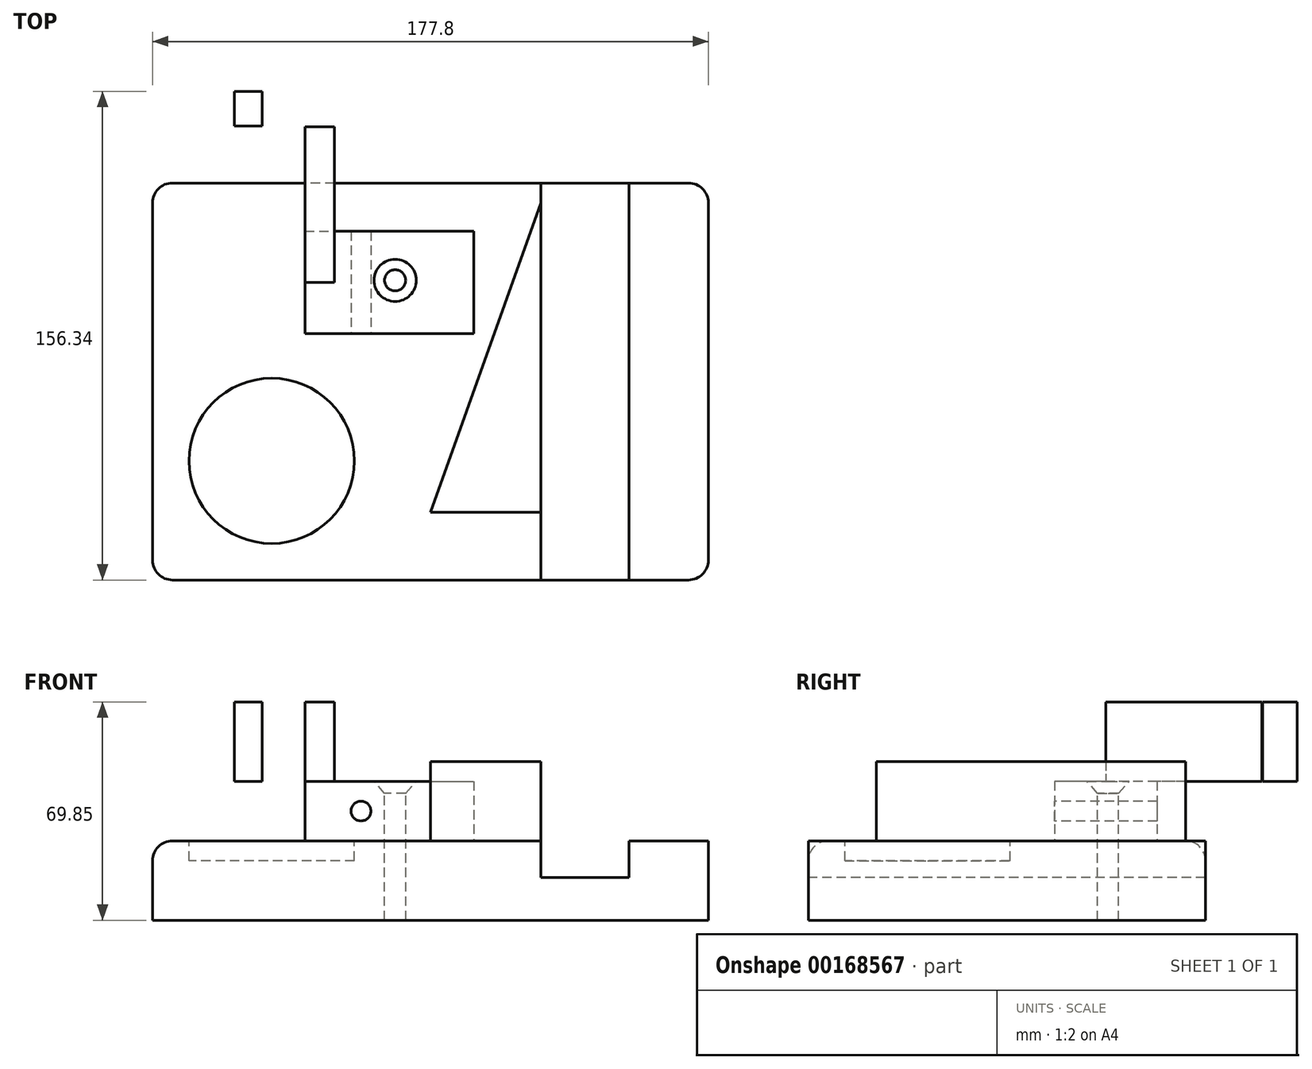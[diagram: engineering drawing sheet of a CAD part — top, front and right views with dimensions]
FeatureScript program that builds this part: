
annotation { "Feature Type Name" : "Feature", "Feature Type Description" : "" }
export const myFeature = defineFeature(function(context is Context, id is Id, definition is map)
    precondition{}
    {
        {
            var Q0;
            Q0=qCreatedBy(makeId("Top.planeOp"),FACE);
            var sketch = newSketch(context, id + "F0", { "sketchPlane" : qUnion([Q0])});
            skLineSegment(sketch, "E0.bottom", {"start": v(82.55, -63.5) * mm, "end": v(-82.55, -63.5) * mm});
            skLineSegment(sketch, "E0.top", {"start": v(82.55, 63.5) * mm, "end": v(-82.55, 63.5) * mm});
            skLineSegment(sketch, "E0.left", {"start": v(88.9, -57.15) * mm, "end": v(88.9, 57.15) * mm});
            skLineSegment(sketch, "E0.right", {"start": v(-88.9, -57.15) * mm, "end": v(-88.9, 57.15) * mm});
            skPoint(sketch, "E0.middle", {"position": v(0, 0) * mm});
            skPoint(sketch, "E1.visualSharp", {"position": v(-88.9, -63.5) * mm});
            skArc(sketch, "E1.filletArc", {"start": v(-88.9, -57.15) * mm, "mid": v(-87.04, -61.64) * mm, "end": v(-82.55, -63.5) * mm});
            skPoint(sketch, "E2.visualSharp", {"position": v(88.9, -63.5) * mm});
            skArc(sketch, "E2.filletArc", {"start": v(82.55, -63.5) * mm, "mid": v(87.04, -61.64) * mm, "end": v(88.9, -57.15) * mm});
            skPoint(sketch, "E3.visualSharp", {"position": v(88.9, 63.5) * mm});
            skArc(sketch, "E3.filletArc", {"start": v(88.9, 57.15) * mm, "mid": v(87.04, 61.64) * mm, "end": v(82.55, 63.5) * mm});
            skPoint(sketch, "E4.visualSharp", {"position": v(-88.9, 63.5) * mm});
            skArc(sketch, "E4.filletArc", {"start": v(-82.55, 63.5) * mm, "mid": v(-87.04, 61.64) * mm, "end": v(-88.9, 57.15) * mm});
            skSolve(sketch);
        }
        {
            var Q0;
            Q0=makeQuery(id+"F0.imprint","IMPRINT",FACE,{"disambiguationData":[TD([[makeQuery(id+"F0.imprint","IMPRINT",EDGE,{"derivedFrom":sQuery(id+"F0.wireOp",EDGE,"E0.bottom")}),-1.0]])]});
            extrude(context, id + "F1", {"entities" : qUnion([Q0]), "depth" : 25.4 * mm});
        }
        {
            var Q0;
            Q0=makeQuery(id+"F1.opExtrude","CAP_FACE",FACE,{"disambiguationData":[OSD([sQuery(id+"F0.wireOp",EDGE,"E0.bottom"),sQuery(id+"F0.wireOp",EDGE,"E0.top"),sQuery(id+"F0.wireOp",EDGE,"E0.left"),sQuery(id+"F0.wireOp",EDGE,"E0.right"),sQuery(id+"F0.wireOp",EDGE,"E1.filletArc"),sQuery(id+"F0.wireOp",EDGE,"E2.filletArc"),sQuery(id+"F0.wireOp",EDGE,"E3.filletArc"),sQuery(id+"F0.wireOp",EDGE,"E4.filletArc")])],"isStart":false});
            var sketch = newSketch(context, id + "F2", { "sketchPlane" : qUnion([Q0])});
            skCircle(sketch, "E5", {"center": v(-50.8, -25.4) * mm, "radius": 26.45 * mm});
            skSolve(sketch);
        }
        {
            var Q0;
            Q0 = qSketchRegion(id + "F2", true);
            extrude(context, id + "F3", {"entities" : qUnion([Q0]), "operationType" : NewBodyOperationType.REMOVE, "oppositeDirection" : true, "depth" : 6.35 * mm});
        }
        {
            var Q0;
            Q0=makeQuery(id+"F1.opExtrude","SWEPT_FACE",FACE,{"disambiguationData":[OSD([sQuery(id+"F0.wireOp",EDGE,"E0.bottom")])]});
            var sketch = newSketch(context, id + "F4", { "sketchPlane" : qUnion([Q0])});
            skLineSegment(sketch, "E6.bottom", {"start": v(63.56, 13.67) * mm, "end": v(35.33, 13.67) * mm});
            skLineSegment(sketch, "E6.top", {"start": v(63.56, 37.13) * mm, "end": v(35.33, 37.13) * mm});
            skLineSegment(sketch, "E6.left", {"start": v(63.56, 13.67) * mm, "end": v(63.56, 37.13) * mm});
            skLineSegment(sketch, "E6.right", {"start": v(35.33, 13.67) * mm, "end": v(35.33, 37.13) * mm});
            skPoint(sketch, "E6.middle", {"position": v(49.44, 25.4) * mm});
            skSolve(sketch);
        }
        {
            var Q0;
            {var subQ0=sQuery(id+"F4.wireOp",EDGE,"E6.bottom");Q0=makeQuery(id+"F4.imprint","IMPRINT",FACE,{"disambiguationData":[TD([[makeQuery(id+"F4.imprint","IMPRINT",EDGE,{"derivedFrom":subQ0}),-1.0]])]});}
            extrude(context, id + "F5", {"entities" : qUnion([Q0]), "operationType" : NewBodyOperationType.REMOVE, "oppositeDirection" : true, "depth" : 127 * mm});
        }
        {
            var Q0;
            {var subQ0=sQuery(id+"F0.wireOp",EDGE,"E1.filletArc");var subQ1=sQuery(id+"F0.wireOp",EDGE,"E0.right");var subQ2=sQuery(id+"F0.wireOp",EDGE,"E0.top");var subQ3=sQuery(id+"F0.wireOp",EDGE,"E0.bottom");var subQ4=sQuery(id+"F0.wireOp",EDGE,"E4.filletArc");Q0=makeQuery(id+"F5.boolean.opBoolean","SPLIT",FACE,{"disambiguationData":[TD([makeQuery(id+"F1.opExtrude","SWEPT_FACE",FACE,{"disambiguationData":[OSD([subQ1])]})])],"derivedFrom":makeQuery(id+"F1.opExtrude","CAP_FACE",FACE,{"disambiguationData":[OSD([subQ3,subQ2,sQuery(id+"F0.wireOp",EDGE,"E0.left"),subQ1,subQ0,sQuery(id+"F0.wireOp",EDGE,"E2.filletArc"),sQuery(id+"F0.wireOp",EDGE,"E3.filletArc"),subQ4])],"isStart":false})});}
            var sketch = newSketch(context, id + "F6", { "sketchPlane" : qUnion([Q0])});
            skLineSegment(sketch, "E7.bottom", {"start": v(-40.18, 48.04) * mm, "end": v(13.9, 48.04) * mm});
            skLineSegment(sketch, "E7.top", {"start": v(-40.18, 15.3) * mm, "end": v(13.9, 15.3) * mm});
            skLineSegment(sketch, "E7.left", {"start": v(-40.18, 48.04) * mm, "end": v(-40.18, 15.3) * mm});
            skLineSegment(sketch, "E7.right", {"start": v(13.9, 48.04) * mm, "end": v(13.9, 15.3) * mm});
            skSolve(sketch);
        }
        {
            var Q0;
            Q0=makeQuery(id+"F6.imprint","IMPRINT",FACE,{"disambiguationData":[TD([[makeQuery(id+"F6.imprint","IMPRINT",EDGE,{"derivedFrom":sQuery(id+"F6.wireOp",EDGE,"E7.bottom")}),-1.0]])]});
            extrude(context, id + "F7", {"entities" : qUnion([Q0]), "operationType" : NewBodyOperationType.ADD, "depth" : 19.05 * mm});
        }
        {
            var Q0;
            {var subQ0=sQuery(id+"F0.wireOp",EDGE,"E0.bottom");var subQ1=sQuery(id+"F0.wireOp",EDGE,"E1.filletArc");Q0=makeQuery(id+"F5.boolean.opBoolean","SPLIT",EDGE,{"disambiguationData":[TD([makeQuery(id+"F1.opExtrude","SWEPT_FACE",FACE,{"disambiguationData":[OSD([subQ1])]})])],"derivedFrom":makeQuery(id+"F1.opExtrude","CAP_EDGE",EDGE,{"disambiguationData":[OSD([subQ0])],"isStart":false})});}
            fillet(context, id + "F8", {"entities" : qUnion([Q0]), "radius" : 6.35 * mm, "tangentPropagation" : true, "allowEdgeOverflow" : false});
        }
        {
            var Q0;
            Q0=makeQuery(id+"F7.opExtrude","CAP_FACE",FACE,{"disambiguationData":[OSD([sQuery(id+"F6.wireOp",EDGE,"E7.bottom"),sQuery(id+"F6.wireOp",EDGE,"E7.top"),sQuery(id+"F6.wireOp",EDGE,"E7.left"),sQuery(id+"F6.wireOp",EDGE,"E7.right")])],"isStart":false});
            var sketch = newSketch(context, id + "F9", { "sketchPlane" : qUnion([Q0])});
            skPoint(sketch, "E8", {"position": v(-11.3, 32.36) * mm});
            skSolve(sketch);
        }
        {
            var Q0;
            Q0=sQuery(id+"F9.wireOp",VERTEX,"E8");
            var Q1;
            Q1=makeQuery(id+"F1.opExtrude","SWEPT_BODY",BODY,{"disambiguationData":[OSD([sQuery(id+"F0.wireOp",EDGE,"E0.bottom"),sQuery(id+"F0.wireOp",EDGE,"E0.top"),sQuery(id+"F0.wireOp",EDGE,"E0.left"),sQuery(id+"F0.wireOp",EDGE,"E0.right"),sQuery(id+"F0.wireOp",EDGE,"E1.filletArc"),sQuery(id+"F0.wireOp",EDGE,"E2.filletArc"),sQuery(id+"F0.wireOp",EDGE,"E3.filletArc"),sQuery(id+"F0.wireOp",EDGE,"E4.filletArc")])]});
            hole(context, id + "F10", {"style" : HoleStyle.C_SINK, "endStyle" : HoleEndStyle.THROUGH, "holeDiameter" : 6.76 * mm, "cSinkDiameter" : 13.5 * mm, "cSinkAngle" : 82 * degree, "locations" : qUnion([Q0]), "scope" : qUnion([Q1]), "isTappedThrough" : true});
        }
        {
            var Q0;
            Q0=makeQuery(id+"F7.opExtrude","SWEPT_FACE",FACE,{"disambiguationData":[OSD([sQuery(id+"F6.wireOp",EDGE,"E7.top")])]});
            var sketch = newSketch(context, id + "F11", { "sketchPlane" : qUnion([Q0])});
            skPoint(sketch, "E9", {"position": v(-22.24, 34.93) * mm});
            skPoint(sketch, "E9.positionSnap0", {"position": v(-40.18, 34.93) * mm});
            skSolve(sketch);
        }
        {
            var Q0;
            Q0=sQuery(id+"F11.wireOp",VERTEX,"E9");
            var Q1;
            Q1=makeQuery(id+"F1.opExtrude","SWEPT_BODY",BODY,{"disambiguationData":[OSD([sQuery(id+"F0.wireOp",EDGE,"E0.bottom"),sQuery(id+"F0.wireOp",EDGE,"E0.top"),sQuery(id+"F0.wireOp",EDGE,"E0.left"),sQuery(id+"F0.wireOp",EDGE,"E0.right"),sQuery(id+"F0.wireOp",EDGE,"E1.filletArc"),sQuery(id+"F0.wireOp",EDGE,"E2.filletArc"),sQuery(id+"F0.wireOp",EDGE,"E3.filletArc"),sQuery(id+"F0.wireOp",EDGE,"E4.filletArc")])]});
            hole(context, id + "F12", {"style" : HoleStyle.SIMPLE, "endStyle" : HoleEndStyle.THROUGH, "holeDiameter" : 6.35 * mm, "locations" : qUnion([Q0]), "scope" : qUnion([Q1]), "isTappedThrough" : true});
        }
        {
            var Q0;
            {var subQ0=sQuery(id+"F0.wireOp",EDGE,"E1.filletArc");var subQ1=sQuery(id+"F0.wireOp",EDGE,"E0.right");var subQ2=sQuery(id+"F0.wireOp",EDGE,"E0.top");var subQ3=sQuery(id+"F0.wireOp",EDGE,"E0.bottom");var subQ4=sQuery(id+"F0.wireOp",EDGE,"E4.filletArc");Q0=makeQuery(id+"F5.boolean.opBoolean","SPLIT",FACE,{"disambiguationData":[TD([makeQuery(id+"F1.opExtrude","SWEPT_FACE",FACE,{"disambiguationData":[OSD([subQ1])]})])],"derivedFrom":makeQuery(id+"F1.opExtrude","CAP_FACE",FACE,{"disambiguationData":[OSD([subQ3,subQ2,sQuery(id+"F0.wireOp",EDGE,"E0.left"),subQ1,subQ0,sQuery(id+"F0.wireOp",EDGE,"E2.filletArc"),sQuery(id+"F0.wireOp",EDGE,"E3.filletArc"),subQ4])],"isStart":false})});}
            var sketch = newSketch(context, id + "F13", { "sketchPlane" : qUnion([Q0])});
            skLineSegment(sketch, "E10", {"start": v(0, -41.78) * mm, "end": v(35.33, 57.15) * mm});
            skLineSegment(sketch, "E11", {"start": v(0, -41.78) * mm, "end": v(35.33, -41.78) * mm});
            skLineSegment(sketch, "E12", {"start": v(35.33, -41.78) * mm, "end": v(35.33, 57.15) * mm});
            skSolve(sketch);
        }
        {
            var Q0;
            Q0=makeQuery(id+"F13.imprint","IMPRINT",FACE,{"disambiguationData":[TD([[makeQuery(id+"F13.imprint","IMPRINT",EDGE,{"derivedFrom":sQuery(id+"F13.wireOp",EDGE,"E10")}),-1.0]])]});
            extrude(context, id + "F16", {"entities" : qUnion([Q0]), "operationType" : NewBodyOperationType.ADD, "depth" : 25.4 * mm});
        }
        {
            var Q0;
            Q0=makeQuery(id+"F7.opExtrude","CAP_FACE",FACE,{"disambiguationData":[OSD([sQuery(id+"F6.wireOp",EDGE,"E7.bottom"),sQuery(id+"F6.wireOp",EDGE,"E7.top"),sQuery(id+"F6.wireOp",EDGE,"E7.left"),sQuery(id+"F6.wireOp",EDGE,"E7.right")])],"isStart":false});
            var sketch = newSketch(context, id + "F14", { "sketchPlane" : qUnion([Q0])});
            skLineSegment(sketch, "E13.bottom", {"start": v(-62.77, 81.78) * mm, "end": v(-53.87, 81.78) * mm});
            skLineSegment(sketch, "E13.top", {"start": v(-62.77, 92.84) * mm, "end": v(-53.87, 92.84) * mm});
            skLineSegment(sketch, "E13.left", {"start": v(-62.77, 81.78) * mm, "end": v(-62.77, 92.84) * mm});
            skLineSegment(sketch, "E13.right", {"start": v(-53.87, 81.78) * mm, "end": v(-53.87, 92.84) * mm});
            skLineSegment(sketch, "E14.bottom", {"start": v(-30.7, 81.52) * mm, "end": v(-40.18, 81.52) * mm});
            skLineSegment(sketch, "E14.top", {"start": v(-30.7, 31.67) * mm, "end": v(-40.18, 31.67) * mm});
            skLineSegment(sketch, "E14.left", {"start": v(-30.7, 81.52) * mm, "end": v(-30.7, 31.67) * mm});
            skLineSegment(sketch, "E14.right", {"start": v(-40.18, 81.52) * mm, "end": v(-40.18, 31.67) * mm});
            skSolve(sketch);
        }
        {
            var Q0;
            Q0 = qSketchRegion(id + "F14", true);
            extrude(context, id + "F15", {"entities" : qUnion([Q0]), "operationType" : NewBodyOperationType.ADD, "depth" : 25.4 * mm});
        }
    });
